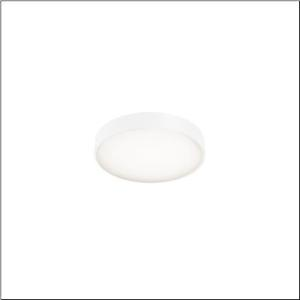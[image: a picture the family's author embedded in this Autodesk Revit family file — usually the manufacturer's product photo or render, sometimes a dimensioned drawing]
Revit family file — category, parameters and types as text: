
# Revit family: round_21_s_51mr34fd0321w
name_source: partatom
category: Lighting Fixtures
units: mm (PartAtom-declared; Revit-internal decimal feet)

## family parameters
Cut with Voids When Loaded = No
Host = Face
Light Source = No
Part Type = Normal
Room Calculation Point = No
Round Connector Dimension = Use Diameter
Shared = No

## types (1)
- Round 21 S (1 x LED, 3750 lm, 30.3 W, 3000K)
    Apparent Load = 30 VA
    CIE Flux Codes = 49 80 96 100 100
    Color Rendering = 80
    Color Temperature = 3000K
    Default Elevation = 1800 mm
    Description = Round 21 S, wall and ceiling luminaire, primary optical cover: cover, of PMMA, opal, light emission: direct distribution, primary light characteristic: symmetric, installation type: suspended mounting, surface-mounted, LED, rated luminous flux: 3.750lm, luminous efficacy: 124lm/W, light colour: 830, colour temperature: 3000K, control gear: DALI 2, with terminal, 5-pole, mains connection: 230V, AC, 50/60Hz, rated input power: 30.3W, housing, of aluminium, coated, white, diameter: 400mm, height: 62mm, protection rating (complete): IP40, insulation class (complete): insulation class I (protective earthing), certification: CE, impact resistance: IK04, permissible operating ambient temperature: -10..+35°C, packaging unit: 1 piece
    Height = 87 mm
    Lamp = 1 x LED
    Lamp Light Flux = 3750 lm
    Lamp Power = 30.3 W
    Lamp count = 1
    Length = 400 mm
    Luminous efficacy = 124 lm/W
    Manufacturer = Siteco
    ModVariant = No
    Model = 51MR34FD0321W
    Mounting Place = Ceiling
    Mounting Type = Surface mounted
    Number of Poles = 1
    OnlyDefault = Yes
    Power Factor = 1
    Product Name = Round 21 S
    Product group = wall and ceiling luminaire | ceiling mounted
    ProductGroupID = 304
    Protection Class = Protection class I
    Protection Degree = IP 40
    RLX_Detail_Level = 1
    RLX_Emergency_Light_Flux = 0 lm
    RLX_Emergency_Type = 0
    RLX_Emergency_Type_DB = No
    RlxData = <blob elided: 9525 chars, md5=71d6d625>
    Socket = socket
    Standby Power = 0 W
    System Light Flux = 3750 lm
    System Power = 30 W
    Type Comments = Product without accessories
    Type Image = l_1258307.jpg
    URL = http://relux.com
    VarID = ---
    Voltage = 0 V
    Weight = 0.00 kg
    Width = 0 mm  [stored 0 ft]

note: [stored X ft] marks values corroborated as IEEE doubles in the binary element streams (Revit-internal decimal feet)

## geometry (parser evidence)
native form markers: Sweep x10
no freeform markers — native parametric forms only
